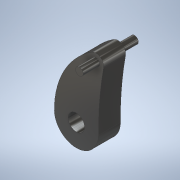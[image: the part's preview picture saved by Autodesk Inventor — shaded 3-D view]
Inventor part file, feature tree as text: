
AUTODESK INVENTOR PART (.ipt)
format: ipt  version: 2021 (Build 250183000, 183)  size: 134,656 bytes
history: native  units: in
note: dims shown in document units (in); Inventor stores cm internally (conversion verified against a paired STEP export)
features: extrude x3, sketch x3, projected_geometry x2, fillet x1
ambient origin geometry x8: Origin, YZ Plane, XZ Plane, XY Plane, X Axis, Y Axis, Z Axis, Center Point
bodies: Solid1 (feature_tree)
feature tree (9):
  extrude  "Extrusion1"  Depth=0.7874in
  fillet  "Fillet2"  Radius=0.1575in
  extrude  "Extrusion2"  Depth=0.0787in TaperAngle=0.0deg
  extrude  "Extrusion3"  Depth=0.0591in TaperAngle=0.0deg
  sketch  "Sketch1"  dims[d0=0.7874in d1=0.7874in d2=0.1575in]
  sketch  "Sketch2"  dims[d3=0.0591in d4=0.0787in d5=0.0in]
  projected_geometry  "Projected Loop1"
  sketch  "Sketch3"  dims[d8=0.0591in d9=0.0in d11=0.0591in d12=0.0in d13=0.0276in d16=0.0276in d17=0.0276in]
  projected_geometry  "Projected Loop2"
